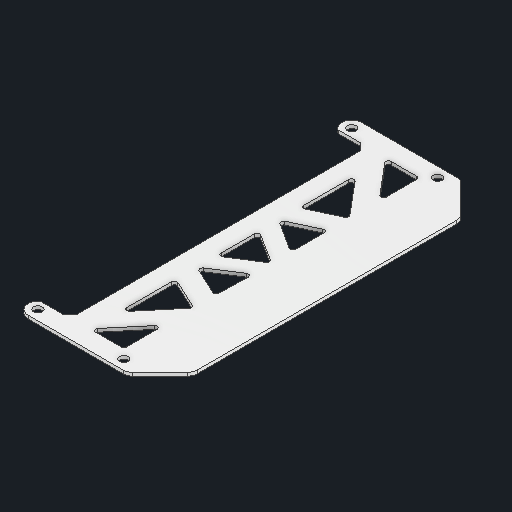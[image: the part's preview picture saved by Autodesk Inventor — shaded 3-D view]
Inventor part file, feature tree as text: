
AUTODESK INVENTOR PART (.ipt)
format: ipt  version: 2025 (Build 290162000, 162)  size: 276,480 bytes
history: native  units: in
note: dims shown in document units (in); Inventor stores cm internally (conversion verified against a paired STEP export)
features: extrude x1, sketch x1, other x1
ambient origin geometry x8: Origin, YZ Plane, XZ Plane, XY Plane, X Axis, Y Axis, Z Axis, Center Point
bodies: Solid1 (feature_tree)
feature tree (3):
  extrude  "Extrusion1"  Depth=0.1875in
  sketch  "Sketch1"  dims[d0=0.165in d3=0.375in d9=0.36in d20=0.05in d21=0.0625in d22=0.0in d24=0.875in d27=0.625in d28=0.625in d29=0.625in d30=0.625in d31=0.1875in]
  other  "Definition1"
